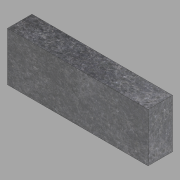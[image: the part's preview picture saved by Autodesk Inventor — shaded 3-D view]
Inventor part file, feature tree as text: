
AUTODESK INVENTOR PART (.ipt)
format: ipt  version: 2022.1 (Build 261234020, 234B)  size: 105,984 bytes
history: native  units: in
note: dims shown in document units (in); Inventor stores cm internally (conversion verified against a paired STEP export)
features: extrude x1, sketch x1
ambient origin geometry x8: Origin, YZ Plane, XZ Plane, XY Plane, X Axis, Y Axis, Z Axis, Center Point
bodies: Solid1 (feature_tree)
feature tree (2):
  extrude  "Extrusion1"  Depth=12.0in
  sketch  "Sketch1"  dims[d0=34.5in d1=12.0in d2=6.0in d3=0.0in]
